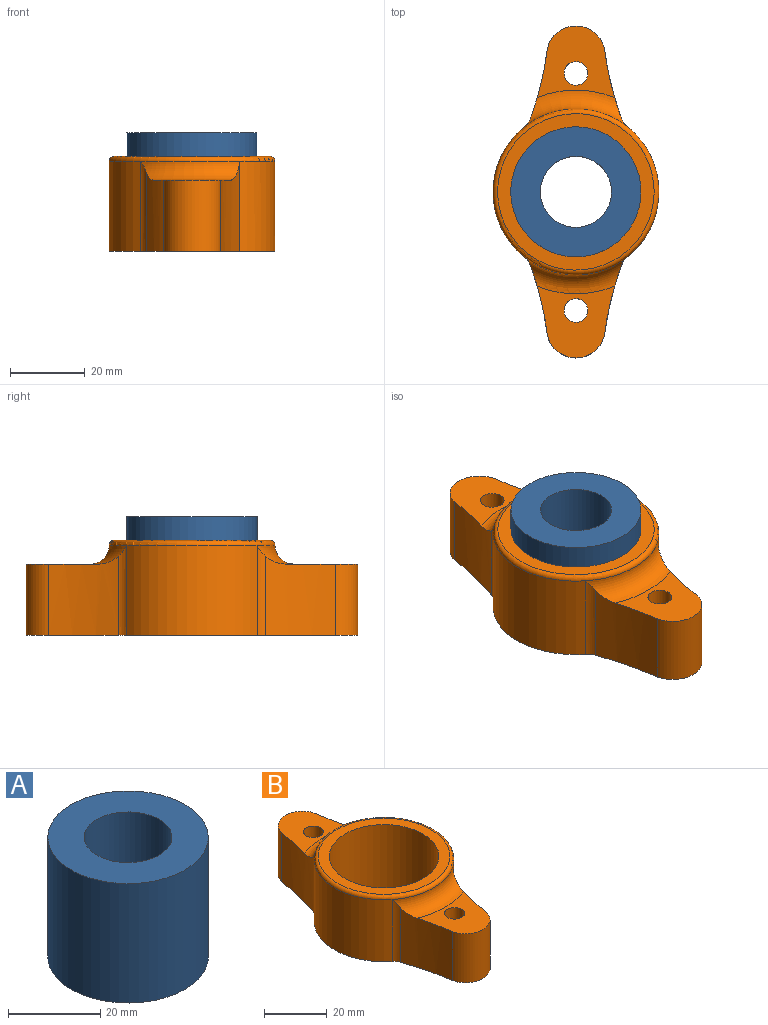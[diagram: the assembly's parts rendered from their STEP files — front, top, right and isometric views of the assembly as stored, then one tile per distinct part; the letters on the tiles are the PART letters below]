
ASSEMBLY  parts=2 mates=1
PART A: 4 faces, bbox 34.9x34.9x31.8 mm
  f0: cylinder r=9.53mm len=31.75mm, axis (0,0,-1), area 1900.2mm2, adj f2,f3
  f1: cylinder r=17.43mm len=34.85mm, axis (0,0,-1), area 3476.5mm2, adj f2,f3
  f2: plane 34.85x34.85mm, normal (0,0,1), area 669mm2, adj f0,f1
  f3: plane 34.85x34.85mm, normal (0,0,-1), area 669mm2, adj f0,f1
PART B: 21 faces, bbox 48.1x88.9x27.7 mm
  f0: cylinder r=22.23mm len=34.83mm, axis (0,0,-1), area 965.9mm2, adj f4,f17,f19,f20
  f1: cylinder r=22.23mm len=35.64mm, axis (0,0,-1), area 998.5mm2, adj f4,f12,f15,f20
  f2: cylinder r=17.43mm len=34.85mm, axis (0,0,-1), area 2781.2mm2, adj f3,f4
  f3: plane 41.91x41.91mm, normal (0,0,1), area 425.4mm2, adj f2,f20
  f4: plane 88.9x44.45mm, normal (0,0,-1), area 1321.1mm2, adj f0,f1,f2,f5,f6,f7,f8,f10
  f5: cylinder r=7.83mm len=19.05mm, axis (0,0,-1), area 398.8mm2, adj f4,f6,f8,f9
  f6: cylinder r=88.9mm len=21.23mm, axis (0,0,-1), area 372.8mm2, adj f4,f5,f9,f16,f17
  f7: cylinder r=3.17mm len=19.05mm, axis (0,0,-1), area 380mm2, adj f4,f9
  f8: cylinder r=88.9mm len=21.23mm, axis (0,0,-1), area 372.8mm2, adj f4,f5,f9,f15,f16
  f9: plane 20.73x19.19mm, normal (0,0,1), area 240.4mm2, adj f5,f6,f7,f8,f16
  f10: cylinder r=88.9mm len=21.23mm, axis (0,0,-1), area 372.8mm2, adj f4,f11,f14,f18,f19
  f11: cylinder r=7.83mm len=19.05mm, axis (0,0,-1), area 398.8mm2, adj f4,f10,f12,f14
  f12: cylinder r=88.9mm len=24.13mm, axis (0,0,-1), area 407mm2, adj f1,f4,f11,f14,f18
  f13: cylinder r=3.17mm len=19.05mm, axis (0,0,-1), area 380mm2, adj f4,f14
  f14: plane 20.73x19.19mm, normal (0,0,1), area 240.4mm2, adj f10,f11,f12,f13,f18
  f15: cylinder r=5.08mm len=24.13mm, axis (0,0,-1), area 63.7mm2, adj f1,f4,f8,f16
  f16: torus R=27.3mm, axis (0,0,1), area 199.6mm2, adj f6,f8,f9,f15,f17,f20
  f17: cylinder r=5.08mm len=24.13mm, axis (0,0,-1), area 63.7mm2, adj f0,f4,f6,f16
  f18: torus R=27.3mm, axis (0,0,1), area 198.2mm2, adj f10,f12,f14,f19,f20
  f19: cylinder r=5.08mm len=24.13mm, axis (0,0,-1), area 63.7mm2, adj f0,f4,f10,f18
  f20: torus R=20.96mm, axis (0,0,1), area 272.8mm2, adj f0,f1,f3,f16,f18
PLACE A at identity
PLACE B at identity
MATE fastened B.f2 <-> A.f0  axis (0,0,-1) through (0,0,0)mm
